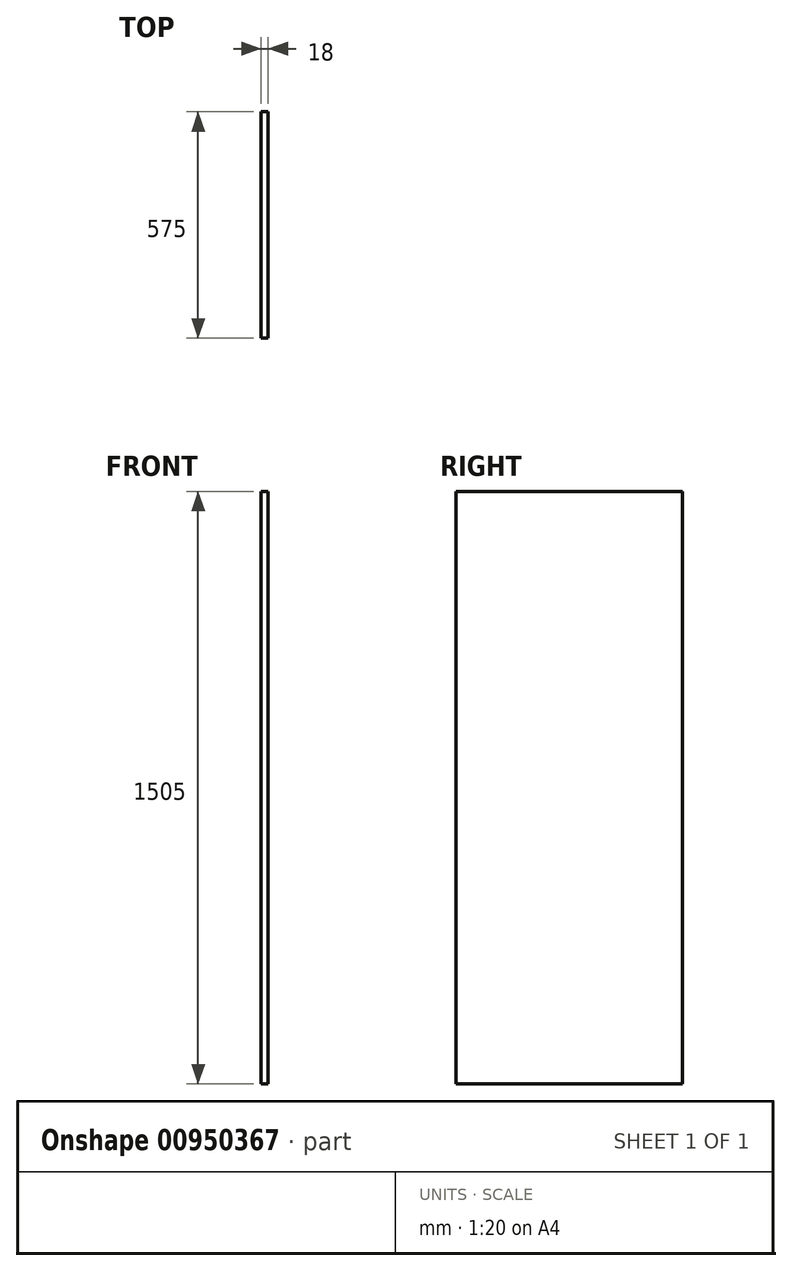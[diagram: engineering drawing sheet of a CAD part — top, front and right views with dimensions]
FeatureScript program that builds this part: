
annotation { "Feature Type Name" : "Feature", "Feature Type Description" : "" }
export const myFeature = defineFeature(function(context is Context, id is Id, definition is map)
    precondition{}
    {
        {
            var Q0;
            Q0=qCreatedBy(makeId("Right.planeOp"),FACE);
            var sketch = newSketch(context, id + "F0", { "sketchPlane" : qUnion([Q0])});
            skLineSegment(sketch, "E0.bottom", {"start": v(0, 0) * mm, "end": v(575, 0) * mm});
            skLineSegment(sketch, "E0.top", {"start": v(0, 1505) * mm, "end": v(575, 1505) * mm});
            skLineSegment(sketch, "E0.left", {"start": v(0, 0) * mm, "end": v(0, 1505) * mm});
            skLineSegment(sketch, "E0.right", {"start": v(575, 0) * mm, "end": v(575, 1505) * mm});
            skSolve(sketch);
        }
        {
            var Q0;
            Q0 = qSketchRegion(id + "F0", true);
            extrude(context, id + "F1", {"entities" : qUnion([Q0]), "depth" : 18 * mm, "offsetDistance" : 25 * mm});
        }
    });
